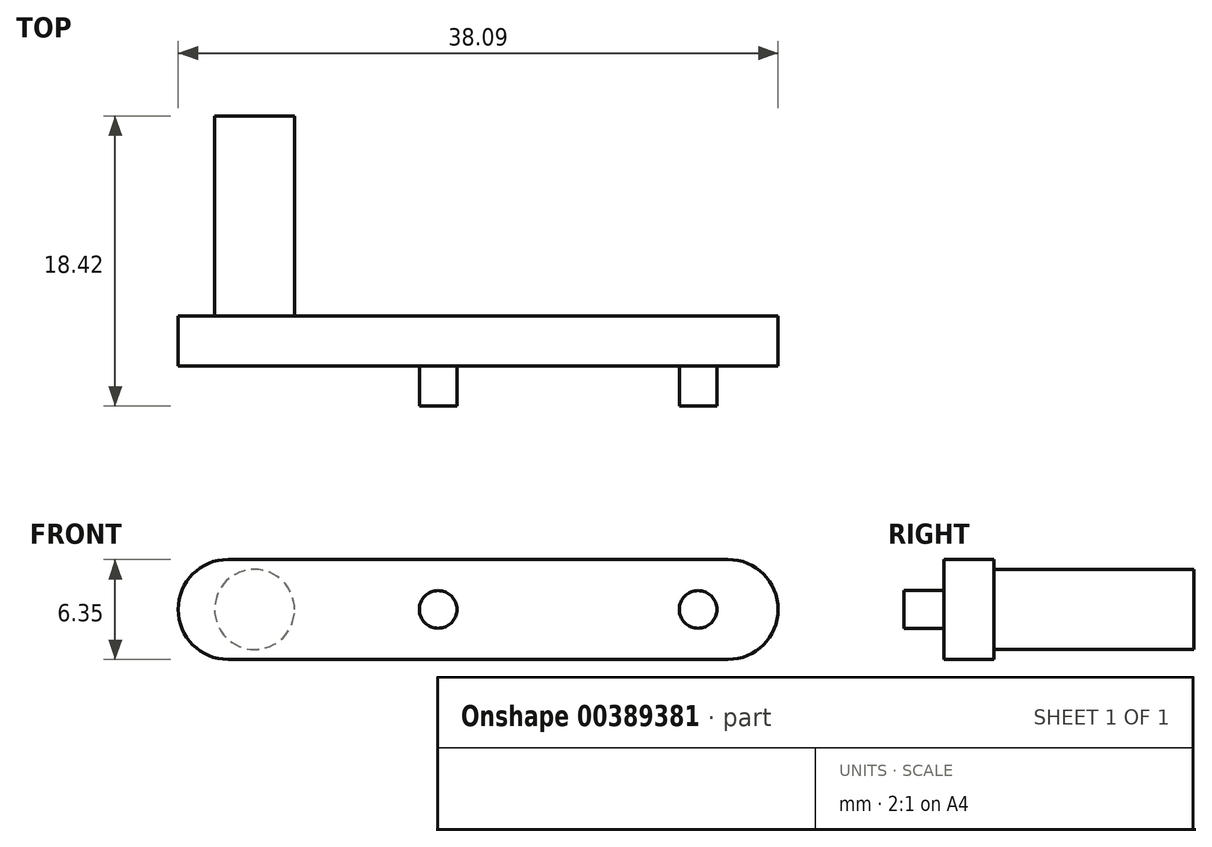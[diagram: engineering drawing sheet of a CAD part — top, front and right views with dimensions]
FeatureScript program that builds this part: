
annotation { "Feature Type Name" : "Feature", "Feature Type Description" : "" }
export const myFeature = defineFeature(function(context is Context, id is Id, definition is map)
    precondition{}
    {
        {
            var Q0;
            Q0=qCreatedBy(makeId("Front.planeOp"),FACE);
            var sketch = newSketch(context, id + "F0", { "sketchPlane" : qUnion([Q0])});
            skArc(sketch, "E0", {"start": v(0, 3.18) * mm, "mid": v(-3.18, 0) * mm, "end": v(0, -3.18) * mm});
            skArc(sketch, "E1", {"start": v(31.75, -3.18) * mm, "mid": v(34.93, 0) * mm, "end": v(31.75, 3.17) * mm});
            skLineSegment(sketch, "E2", {"start": v(0, 3.18) * mm, "end": v(31.75, 3.18) * mm});
            skLineSegment(sketch, "E3", {"start": v(0, -3.17) * mm, "end": v(31.75, -3.17) * mm});
            skSolve(sketch);
        }
        {
            var Q0;
            Q0 = qSketchRegion(id + "F0", true);
            extrude(context, id + "F1", {"entities" : qUnion([Q0]), "depth" : 3.17 * mm});
        }
        {
            var Q0;
            Q0=makeQuery(id+"F1.opExtrude","CAP_FACE",FACE,{"disambiguationData":[OSD([sQuery(id+"F0.wireOp",EDGE,"E0"),sQuery(id+"F0.wireOp",EDGE,"E1"),sQuery(id+"F0.wireOp",EDGE,"E2"),sQuery(id+"F0.wireOp",EDGE,"E3")])],"isStart":false});
            var sketch = newSketch(context, id + "F2", { "sketchPlane" : qUnion([Q0])});
            skCircle(sketch, "E4", {"center": v(13.34, 0) * mm, "radius": 1.2 * mm});
            skCircle(sketch, "E5", {"center": v(29.85, 0) * mm, "radius": 1.2 * mm});
            skSolve(sketch);
        }
        {
            var Q0;
            Q0 = qSketchRegion(id + "F2", true);
            extrude(context, id + "F3", {"entities" : qUnion([Q0]), "operationType" : NewBodyOperationType.ADD, "depth" : 2.54 * mm});
        }
        {
            var Q0;
            Q0=makeQuery(id+"F1.opExtrude","CAP_FACE",FACE,{"disambiguationData":[OSD([sQuery(id+"F0.wireOp",EDGE,"E0"),sQuery(id+"F0.wireOp",EDGE,"E1"),sQuery(id+"F0.wireOp",EDGE,"E2"),sQuery(id+"F0.wireOp",EDGE,"E3")])],"isStart":true});
            var sketch = newSketch(context, id + "F4", { "sketchPlane" : qUnion([Q0])});
            skCircle(sketch, "E6", {"center": v(-1.68, 0) * mm, "radius": 2.54 * mm});
            skSolve(sketch);
        }
        {
            var Q0;
            Q0 = qSketchRegion(id + "F4", true);
            extrude(context, id + "F5", {"entities" : qUnion([Q0]), "operationType" : NewBodyOperationType.ADD, "depth" : 12.7 * mm});
        }
    });
